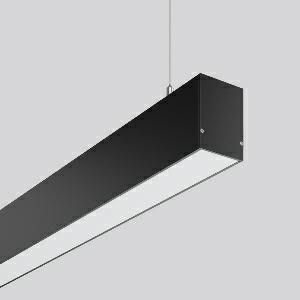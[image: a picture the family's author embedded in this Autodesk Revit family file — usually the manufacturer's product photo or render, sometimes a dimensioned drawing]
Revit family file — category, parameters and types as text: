
# Revit family: less_is_more_50_312317_003_1_09c8
name_source: partatom
category: Lighting Fixtures
units: mm (PartAtom-declared; Revit-internal decimal feet)

## family parameters
Cut with Voids When Loaded = No
Host = Face
Light Source = No
Part Type = Normal
Room Calculation Point = No
Round Connector Dimension = Use Diameter
Shared = No

## types (1)
- LESS IS MORE 50 (1 x LED Modul 840, 4000 lm, 4000)
    Apparent Load = 34 VA
    CIE Flux Codes = 49 80 96 63 100
    Color Rendering = 80
    Color Temperature = 4000
    Default Elevation = 1800 mm
    Description = Series: LESS IS MORE 50
Linear pendant luminaire for aesthetically sophisticated lighting. Housing: extruded aluminium profile, powder-coated. End cap aluminium powder-coated. Canopy made of aluminium, powder-coated. Diffuser made of non-yellowing plastic (PMMA), opal. Direct 65%, indirect 35% light emission. Suitable for pendant. 2-point steel cable suspension freely positionable and infinitely height-adjustable. Special lengths available on request. LED unit with integrated converter interchangeable and removable. Suitable for through-wiring. With sensors or as a safety luminaire on request. 
Colour: deep black, matt (RAL 9005)
Length: 847 mm
Width: 57 mm
Height: 75 mm
Suspension length: 2000 mm
Lamp: LED
Socket: without socket
Colour temperature: 4000K
Colour rendering index (CRI): 80
Light source: LED
Socket lamp2: Without base
Colour temperature: 4000K
System power: 34 W
Rated luminous flux: 4000 lm
Luminous efficiency: 118 lm/W
Control gear: Regulated power supply
Control gear: Regulated power supply
Protection class: I
Type of protection: IP 20
    Height = 75 mm
    Lamp = 1 x LED Modul 840
    Lamp Light Flux = 4000 lm
    Lamp count = 1
    Length = 847 mm
    Lifetime = 50000 h
    Luminous efficacy = 118 lm/W
    Manufacturer = RZB
    ModVariant = No
    Model = 312317.003.1
    Mounting Place = Ceiling
    Mounting Type = Pendant
    Number of Poles = 1
    OnlyDefault = Yes
    Power Factor = 1
    Product Name = LESS IS MORE 50
    Product group = Pendant LED linear luminaires
    ProductGroupID = 907
    Protection Class = Protection class I
    Protection Degree = IP 20
    RLX_Detail_Level = 1
    RLX_Emergency_Light_Flux = 0 lm
    RLX_Emergency_Type = 0
    RLX_Emergency_Type_DB = No
    RlxData = <blob elided: 39829 chars, md5=c04155c5>
    Socket = socket
    Standby Power = 0 W
    System Light Flux = 4000 lm
    System Power = 34 W
    Type Comments = Product without accessories
    Type Image = 312318.003.jpg
    URL = http://relux.com
    VarID = ---
    Voltage = 230 V
    Voltage Range = 220-240 V
    Weight = 0.00 kg
    Width = 57 mm

## geometry (parser evidence)
native form markers: Blend x4, Sweep x11
no freeform markers — native parametric forms only
